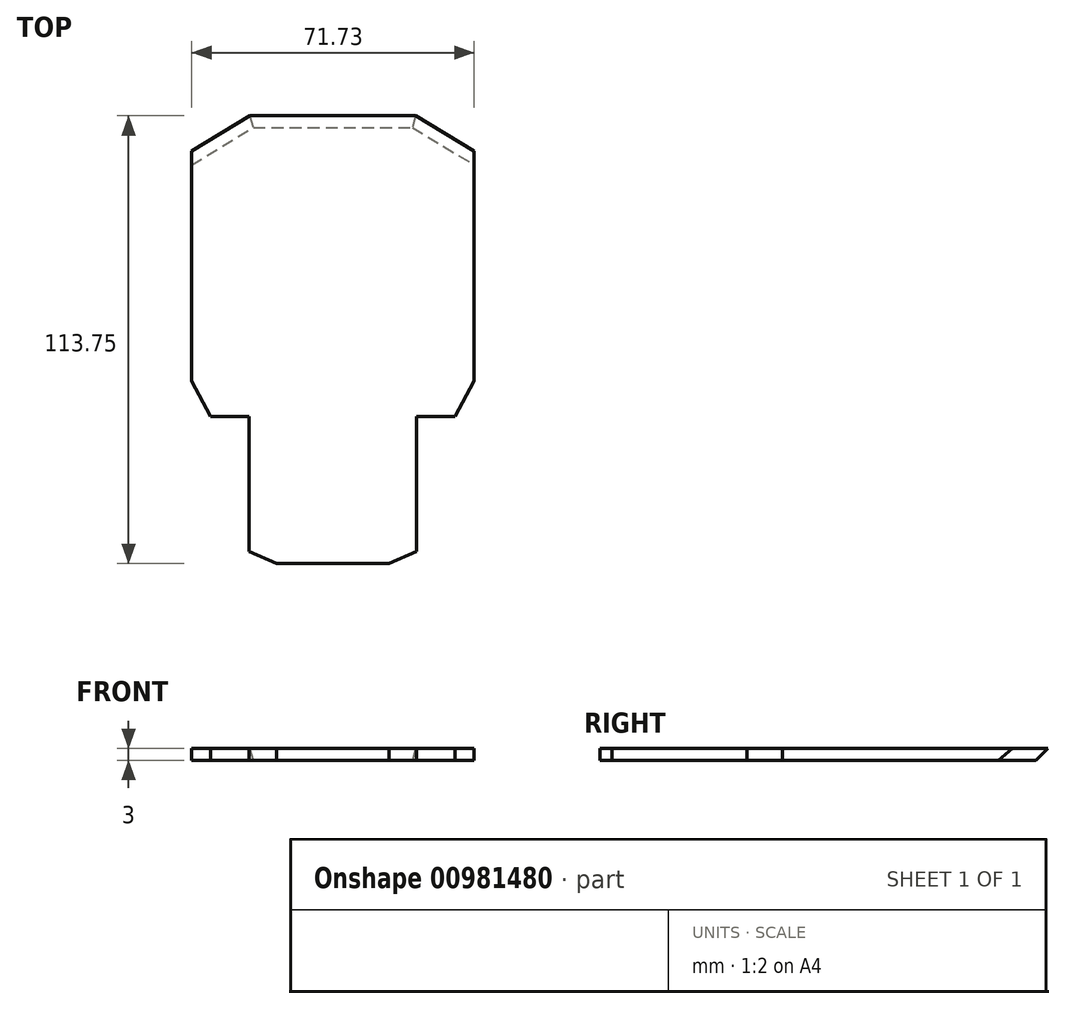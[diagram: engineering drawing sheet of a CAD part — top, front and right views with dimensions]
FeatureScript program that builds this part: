
annotation { "Feature Type Name" : "Feature", "Feature Type Description" : "" }
export const myFeature = defineFeature(function(context is Context, id is Id, definition is map)
    precondition{}
    {
        {
            var Q0;
            Q0=qCreatedBy(makeId("Top.planeOp"),FACE);
            var sketch = newSketch(context, id + "F0", { "sketchPlane" : qUnion([Q0])});
            skLineSegment(sketch, "E0.bottom", {"start": v(7.5, 47.8) * mm, "end": v(50.67, 47.8) * mm});
            skLineSegment(sketch, "E0.top", {"start": v(14.84, -67.95) * mm, "end": v(43.33, -67.95) * mm});
            skLineSegment(sketch, "E0.left", {"start": v(-6.78, 39.13) * mm, "end": v(-6.78, -21.66) * mm});
            skLineSegment(sketch, "E0.right", {"start": v(64.95, 39.13) * mm, "end": v(64.95, -21.66) * mm});
            skLineSegment(sketch, "E1.bottom", {"start": v(-1.98, -30.6) * mm, "end": v(7.82, -30.6) * mm});
            skLineSegment(sketch, "E1.right", {"start": v(7.82, -30.6) * mm, "end": v(7.82, -64.95) * mm});
            skLineSegment(sketch, "E2", {"start": v(29.08, 47.8) * mm, "end": v(29.08, -67.95) * mm, "construction": true});
            skLineSegment(sketch, "E3.MirrorCS", {"start": v(50.35, -30.6) * mm, "end": v(50.35, -64.95) * mm});
            skLineSegment(sketch, "E4.MirrorCS", {"start": v(60.15, -30.6) * mm, "end": v(50.35, -30.6) * mm});
            skPoint(sketch, "E5.orphan", {"position": v(-6.78, -67.95) * mm});
            skPoint(sketch, "E6.orphan", {"position": v(64.95, -67.95) * mm});
            skLineSegment(sketch, "E7", {"start": v(-6.78, 39.13) * mm, "end": v(7.5, 47.8) * mm});
            skLineSegment(sketch, "E8.MirrorCS", {"start": v(64.95, 39.13) * mm, "end": v(50.67, 47.8) * mm});
            skPoint(sketch, "E9.orphan", {"position": v(-6.78, 47.8) * mm});
            skPoint(sketch, "E10.orphan", {"position": v(64.95, 47.8) * mm});
            skLineSegment(sketch, "E11", {"start": v(-6.78, -21.66) * mm, "end": v(-1.98, -30.6) * mm});
            skLineSegment(sketch, "E12.MirrorCS", {"start": v(64.95, -21.66) * mm, "end": v(60.15, -30.6) * mm});
            skPoint(sketch, "E13.orphan", {"position": v(-6.78, -30.6) * mm});
            skPoint(sketch, "E14.orphan", {"position": v(64.95, -30.6) * mm});
            skLineSegment(sketch, "E15", {"start": v(7.82, -64.95) * mm, "end": v(14.84, -67.95) * mm});
            skLineSegment(sketch, "E16.MirrorCS", {"start": v(50.35, -64.95) * mm, "end": v(43.33, -67.95) * mm});
            skPoint(sketch, "E17.orphan", {"position": v(7.82, -67.95) * mm});
            skPoint(sketch, "E18.orphan", {"position": v(50.35, -67.95) * mm});
            skSolve(sketch);
        }
        {
            var Q0;
            Q0=makeQuery(id+"F0.imprint","IMPRINT",FACE,{"disambiguationData":[TD([[makeQuery(id+"F0.imprint","IMPRINT",EDGE,{"derivedFrom":sQuery(id+"F0.wireOp",EDGE,"E0.bottom")}),-1.0]])]});
            extrude(context, id + "F1", {"entities" : qUnion([Q0]), "depth" : 3 * mm, "offsetDistance" : 25 * mm});
        }
        {
            var Q0;
            Q0=makeQuery(id+"F1.opExtrude","CAP_EDGE",EDGE,{"disambiguationData":[OSD([sQuery(id+"F0.wireOp",EDGE,"E8.MirrorCS")])],"isStart":true});
            var Q1;
            Q1=makeQuery(id+"F1.opExtrude","CAP_EDGE",EDGE,{"disambiguationData":[OSD([sQuery(id+"F0.wireOp",EDGE,"E0.bottom")])],"isStart":true});
            var Q2;
            Q2=makeQuery(id+"F1.opExtrude","CAP_EDGE",EDGE,{"disambiguationData":[OSD([sQuery(id+"F0.wireOp",EDGE,"E7")])],"isStart":true});
            chamfer(context, id + "F2", {"entities" : qUnion([Q0, Q1, Q2]), "width" : 5 * mm, "tangentPropagation" : true});
        }
    });
